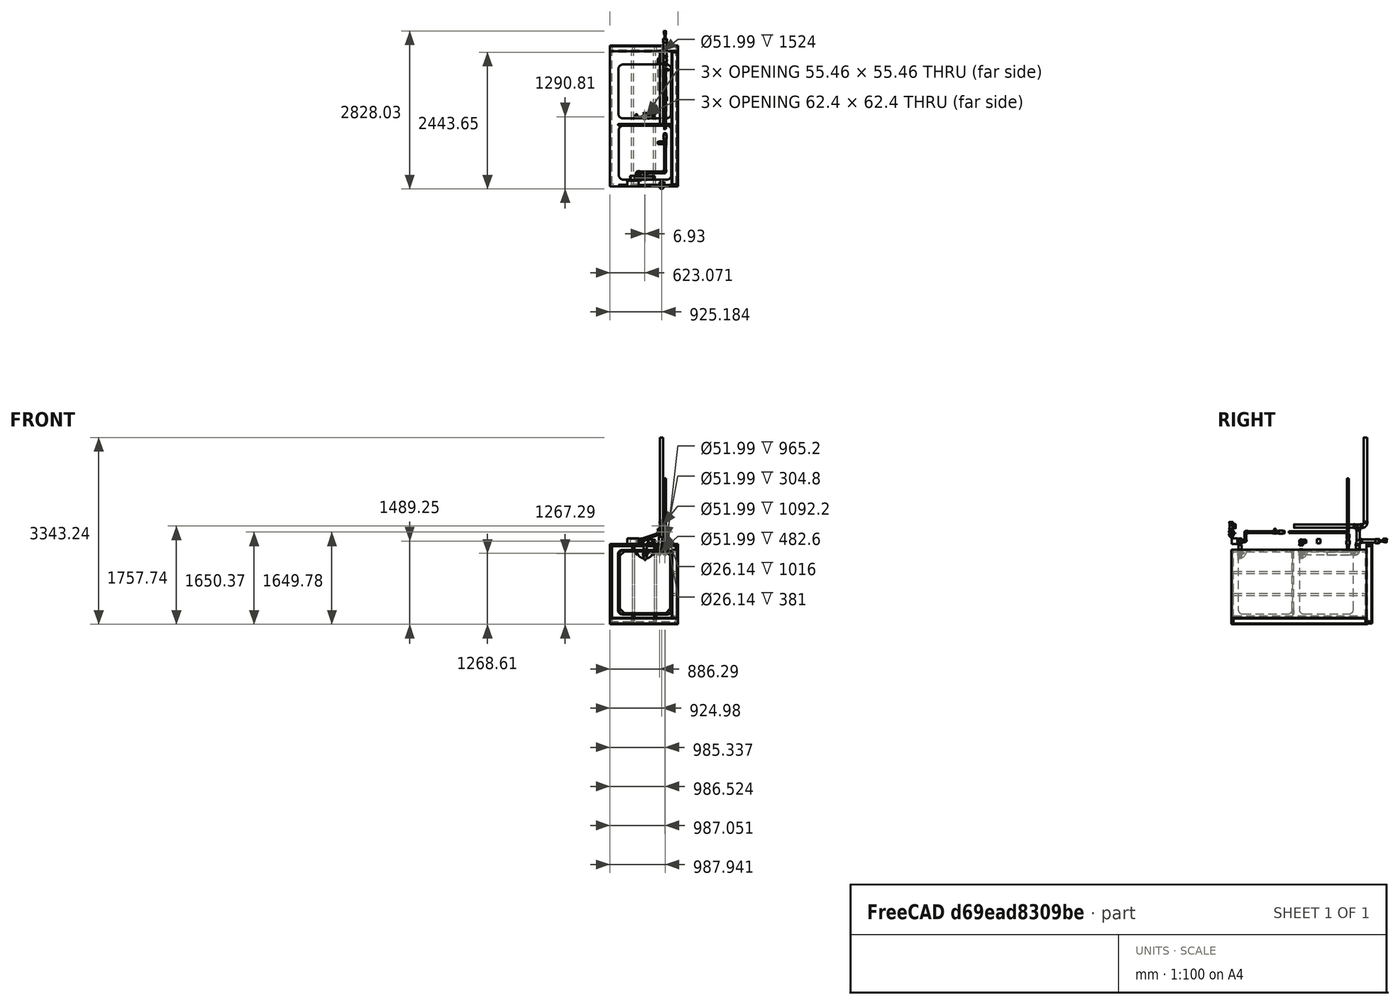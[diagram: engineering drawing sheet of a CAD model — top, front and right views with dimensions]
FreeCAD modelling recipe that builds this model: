
FCSTD DOCUMENT  (FreeCAD 0.17R13125 (Git))
Label: biodigester with case
License: All rights reserved
LicenseURL: http://en.wikipedia.org/wiki/All_rights_reserved
objects: Part::FeaturePython×50, Part::Feature×29, Part::Compound×2, Part::Box×1, Part::Cylinder×1, Part::Cut×1, App::MeasureDistance×1
note: 84 computed .brp shape members not serialized (recipe doc carries the construction recipe); baked Part::Feature solids carry a one-line shape summary decoded from their .brp

FEATURE [Part::Feature] Part__Feature  label="Waste Elbow 2"
  Placement = pos=(292.227,-26.6835,668.11) rot=(0,1,0;1.5708rad)
  shape: bbox 74.37 x 115.1 x 115.1 mm, 30 faces (baked)
FEATURE [Part::Feature] Part__Feature016  label="Bottom Tee"
  Placement = pos=(-0.557936,130.762,666.483) rot=(0,0.707107,-0.707107;3.14159rad)
  shape: bbox 131.8 x 74.37 x 115.1 mm, 49 faces (baked)
FEATURE [Part::Feature] Part__Feature017  label="Tee to pump Bushing"
  Placement = pos=(-111.322,130.762,666.828) rot=(0,1,0;3.14159rad)
  shape: bbox 44.45 x 100.1 x 100.1 mm, 12 faces (baked)
FEATURE [Part::Feature] pipe__solid_  label="Pipe to Pump"
  Placement = pos=(-130.733,130.762,666.483) rot=(0,1,0;1.5708rad)
  shape: bbox 76.2 x 60.33 x 60.33 mm, 4 faces (baked)
FEATURE [Part::FeaturePython] Clone001  label="Top Tote"  # WARN: FeaturePython — macro-defined, semantics opaque (R4)
  AttacherType = Attacher::AttachEngine3D
  Fuse = false
  MapMode = -1
  Placement = pos=(-8.60907,1092.95,-66.7069) rot=(0,0,1;0rad)
  Scale = (1,1,1)
FEATURE [Part::FeaturePython] Clone  label="Bottom Tote"  # WARN: FeaturePython — macro-defined, semantics opaque (R4)
  AttacherType = Attacher::AttachEngine3D
  Fuse = false
  MapMode = -1
  Placement = pos=(-1.679,-2.02686,-66.7069) rot=(0,0,1;0rad)
  Scale = (1,1,1)
FEATURE [Part::FeaturePython] Clone002  label="Macerator Lift Pump001"  # WARN: FeaturePython — macro-defined, semantics opaque (R4)
  AttacherType = Attacher::AttachEngine3D
  Fuse = false
  MapMode = -1
  Placement = pos=(-116.31,128.621,668.824) rot=(0,-1,0;1.5708rad)
  Scale = (1,1,1)
FEATURE [Part::Box] Box  label="C"
  AttacherType = Attacher::AttachEngine3D
  Height = 101.6
  Length = 203.2
  Placement = pos=(-317.752,-21.356,614.794) rot=(0,0,1;0rad)
  Width = 101.6
FEATURE [Part::FeaturePython] Clone003  label="bottom 2" tee"  # Draft clone (typed FeaturePython)
  Objects = -> [Part__Feature016]
  Placement = pos=(144.238,131.333,666.304) rot=(0,0.99998,-0.006329;3.14159rad)
  Scale = (1,1,1)
FEATURE [Part::FeaturePython] Clone004  label="Waste 2" elbow"  # Draft clone (typed FeaturePython)
  Objects = -> [Part__Feature]
  Placement = pos=(293.076,131.009,668.16) rot=(1,0,0;3.14159rad)
  Scale = (1,1,1)
FEATURE [Part::Feature] pipe__solid_001  label="Waste Pipe"
  Placement = pos=(292.227,-26.6835,745.898) rot=(0,0,1;0rad)
  shape: bbox 60.33 x 60.33 x 1524 mm, 4 faces (baked)
FEATURE [Part::FeaturePython] Clone007  label="Top Elbow 1"  # WARN: FeaturePython — macro-defined, semantics opaque (R4)
  Placement = pos=(-7.45656,1223.7,666.865) rot=(0,0.707107,-0.707107;3.14159rad)
  Scale = (1,1,1)
FEATURE [Part::Feature] pipe__solid_002  label="Up pipe"
  Placement = pos=(145.662,1171.16,668.091) rot=(1,0,0;1.5708rad)
  shape: bbox 60.33 x 965.2 x 60.33 mm, 4 faces (baked)
FEATURE [Part::Feature] pipe__solid_003  label="Drain stub 2""
  Placement = pos=(127.656,129.545,666.053) rot=(0,-1,0;1.5708rad)
  shape: bbox 76.2 x 60.33 x 60.33 mm, 4 faces (baked)
FEATURE [Part::FeaturePython] Clone010  label="Top Cleanout Tee"  # Draft clone (typed FeaturePython)
  Objects = -> [Clone003]
  Placement = pos=(147.691,1224.35,665.907) rot=(0.006329,0.006329,0.99996;1.57084rad)
  Scale = (1,1,1)
FEATURE [Part::FeaturePython] Clone011  label="2" valve"  # WARN: FeaturePython — macro-defined, semantics opaque (R4)
  Scale = (1,1,1)
FEATURE [Part::Feature] pipe__solid_004  label="pipe (solid)"
  Placement = pos=(254.718,597.22,447.562) rot=(-1,0,0;1.5708rad)
  shape: bbox 60.33 x 482.6 x 60.33 mm, 4 faces (baked)
FEATURE [Part::FeaturePython] Clone013  label="Waste 2" elbow001"  # Draft clone (typed FeaturePython)
  AttacherType = Attacher::AttachEngine3D
  Fuse = false
  MapMode = -1
  Objects = -> [Clone004]
  Placement = pos=(293.076,131.009,668.16) rot=(1,0,0;3.14159rad)
  Scale = (1,1,1)
FEATURE [Part::FeaturePython] Clone015  label="Overflow Tee"  # Draft clone (typed FeaturePython)
  AttacherType = Attacher::AttachEngine3D
  Fuse = false
  MapMode = -1
  Objects = -> [Clone010]
  Placement = pos=(293.218,1148.28,936.413) rot=(-0.564425,-0.564425,0.602369;2.05727rad)
  Scale = (1,1,1)
FEATURE [Part::FeaturePython] Clone014  label="Gas Elbow"  # Draft clone (typed FeaturePython)
  AttacherType = Attacher::AttachEngine3D
  Fuse = false
  MapMode = -1
  Objects = -> [Clone013]
  Placement = pos=(355.154,1146.76,448.742) rot=(0.707107,0,-0.707107;3.14159rad)
  Scale = (1,1,1)
FEATURE [Part::FeaturePython] Clone016  label="Overflow Tee 2"  # Draft clone (typed FeaturePython)
  AttacherType = Attacher::AttachEngine3D
  Fuse = false
  MapMode = -1
  Objects = -> [Clone015]
  Placement = pos=(292.224,-26.2791,935.756) rot=(0.006329,0.99996,-0.006329;1.57084rad)
  Scale = (1,1,1)
FEATURE [Part::FeaturePython] Clone017  label="Gas Downpipe"  # Draft clone (typed FeaturePython)
  AttacherType = Attacher::AttachEngine3D
  Fuse = false
  MapMode = -1
  Objects = -> [pipe__solid_002]
  Placement = pos=(354.629,1072.64,448.875) rot=(1,0,0;1.5708rad)
  Scale = (1,1,1)
FEATURE [Part::Cylinder] Cylinder
  Angle = 360
  AttacherType = Attacher::AttachEngine3D
  Height = 127
  Placement = pos=(353.737,1033.4,387.109) rot=(0,0,1;0rad)
  Radius = 21.59
FEATURE [Part::Cut] Cut  label="Gas Cut Pipe"
  Base = -> Clone017
  Refine = true
  Tool = -> Cylinder
FEATURE [Part::FeaturePython] Clone018  label="Gas Elbow 2"  # Draft clone (typed FeaturePython)
  AttacherType = Attacher::AttachEngine3D
  Fuse = false
  MapMode = -1
  Objects = -> [Clone014]
  Placement = pos=(355.824,1146.66,669.178) rot=(0,-1,0;1.5708rad)
  Scale = (1,1,1)
FEATURE [Part::Feature] pipe__solid_005  label="Gas Out Stub"
  Placement = pos=(354.597,1146.35,508.528) rot=(0,0,1;0rad)
  shape: bbox 60.33 x 60.33 x 101.6 mm, 4 faces (baked)
FEATURE [Part::Feature] pipe__solid_006  label="Gas Out"
  Placement = pos=(355.816,1528.26,669.516) rot=(1,0,0;1.5708rad)
  shape: bbox 60.33 x 304.8 x 60.33 mm, 4 faces (baked)
FEATURE [Part::Feature] pipe__solid_007  label="Gas Out 1/2""
  Placement = pos=(355.659,1655.7,669.196) rot=(1,0,0;1.5708rad)
  shape: bbox 21.34 x 152.4 x 21.34 mm, 4 faces (baked)
FEATURE [Part::Feature] pipe__solid_008  label="Effluent Down Pipe"
  Placement = pos=(293.409,0.694018,938.006) rot=(-1,0,0;1.5708rad)
  shape: bbox 60.33 x 1092 x 60.33 mm, 4 faces (baked)
FEATURE [Part::Feature] pipe__solid_009  label="Effluent Horizontal Pipe"
  Placement = pos=(261.486,1148.14,525.53) rot=(0,1,0;0.069813rad)
  shape: bbox 86.76 x 60.33 x 384.3 mm, 4 faces (baked)
FEATURE [Part::FeaturePython] Clone025  label="Gas Out001"  # Draft clone (typed FeaturePython)
  AttacherType = Attacher::AttachEngine3D
  Fuse = false
  MapMode = -1
  Objects = -> [pipe__solid_006]
  Placement = pos=(355.816,1528.26,669.516) rot=(1,0,0;1.5708rad)
  Scale = (1,1,1)
FEATURE [Part::FeaturePython] Clone026  label="Gas Out 1/2"001"  # Draft clone (typed FeaturePython)
  AttacherType = Attacher::AttachEngine3D
  Fuse = false
  MapMode = -1
  Objects = -> [pipe__solid_007]
  Placement = pos=(355.659,1620.29,670.928) rot=(1,0,0;1.5708rad)
  Scale = (1,1,1)
FEATURE [Part::FeaturePython] Clone027  label="Gas Elbow 003"  # Draft clone (typed FeaturePython)
  AttacherType = Attacher::AttachEngine3D
  Fuse = false
  MapMode = -1
  Objects = -> [Clone018]
  Placement = pos=(355.824,1146.66,669.178) rot=(0,-1,0;1.5708rad)
  Scale = (1,1,1)
FEATURE [Part::FeaturePython] Clone028  label="Gas Elbow 004"  # Draft clone (typed FeaturePython)
  AttacherType = Attacher::AttachEngine3D
  Fuse = false
  MapMode = -1
  Objects = -> [Clone018]
  Placement = pos=(355.824,1146.66,669.178) rot=(0,-1,0;1.5708rad)
  Scale = (1,1,1)
FEATURE [Part::FeaturePython] Clone029  label="Gas Out Stub001"  # Draft clone (typed FeaturePython)
  AttacherType = Attacher::AttachEngine3D
  Fuse = false
  MapMode = -1
  Objects = -> [pipe__solid_005]
  Placement = pos=(354.597,1146.35,508.528) rot=(0,0,1;0rad)
  Scale = (1,1,1)
FEATURE [Part::FeaturePython] Clone030  label="Gas Elbow001"  # Draft clone (typed FeaturePython)
  AttacherType = Attacher::AttachEngine3D
  Fuse = false
  MapMode = -1
  Objects = -> [Clone014]
  Placement = pos=(355.154,1146.76,448.742) rot=(0.707107,0,-0.707107;3.14159rad)
  Scale = (1,1,1)
FEATURE [Part::FeaturePython] Clone031  label="Gas Cut Pipe001"  # Draft clone (typed FeaturePython)
  AttacherType = Attacher::AttachEngine3D
  Fuse = false
  MapMode = -1
  Objects = -> [Cut]
  Scale = (1,1,1)
FEATURE [Part::Compound] Compound001  label="Top Gas Out"
  Links = -> [Clone031,Clone030,Clone029,Clone028,Clone027,Clone026,Clone025]
  Placement = pos=(-0.971954,1087.98,0) rot=(0,0,1;0rad)
FEATURE [Part::FeaturePython] Clone032  label="Effluent Elbow Orig"  # Draft clone (typed FeaturePython)
  AttacherType = Attacher::AttachEngine3D
  Fuse = false
  MapMode = -1
  Objects = -> [Clone014]
  Placement = pos=(254.97,1146.76,448.515) rot=(-0.681998,0,0.731354;3.14159rad)
  Scale = (1,1,1)
FEATURE [Part::FeaturePython] Clone033  label="pipe (solid)001"  # Draft clone (typed FeaturePython)
  AttacherType = Attacher::AttachEngine3D
  Fuse = false
  MapMode = -1
  Objects = -> [pipe__solid_004]
  Placement = pos=(254.718,597.22,447.562) rot=(-1,0,0;1.5708rad)
  Scale = (1,1,1)
FEATURE [Part::FeaturePython] Clone034  label="Effluent Elbow Orig001"  # Draft clone (typed FeaturePython)
  AttacherType = Attacher::AttachEngine3D
  Fuse = false
  MapMode = -1
  Objects = -> [Clone032]
  Placement = pos=(254.97,1146.76,448.515) rot=(-0.681998,0,0.731354;3.14159rad)
  Scale = (1,1,1)
FEATURE [Part::FeaturePython] Clone035  label="Effluent Horizontal Pipe001"  # Draft clone (typed FeaturePython)
  AttacherType = Attacher::AttachEngine3D
  Fuse = false
  MapMode = -1
  Objects = -> [pipe__solid_009]
  Placement = pos=(261.486,1148.14,525.53) rot=(0,1,0;0.069813rad)
  Scale = (1,1,1)
FEATURE [Part::FeaturePython] Clone036  label="Overflow Tee001"  # Draft clone (typed FeaturePython)
  AttacherType = Attacher::AttachEngine3D
  Fuse = false
  MapMode = -1
  Objects = -> [Clone015]
  Placement = pos=(293.218,1148.28,936.413) rot=(-0.564425,-0.564425,0.602369;2.05727rad)
  Scale = (1,1,1)
FEATURE [Part::FeaturePython] Clone037  label="Effluent Down Pipe001"  # Draft clone (typed FeaturePython)
  AttacherType = Attacher::AttachEngine3D
  Fuse = false
  MapMode = -1
  Objects = -> [pipe__solid_008]
  Placement = pos=(293.409,0.694018,938.006) rot=(-1,0,0;1.5708rad)
  Scale = (1,1,1)
FEATURE [Part::Compound] Compound  label="Top Effluent"
  Links = -> [Clone037,Clone036,Clone035,Clone034,Clone033]
  Placement = pos=(-0.108429,1095.21,0) rot=(0,0,1;0rad)
FEATURE [Part::Feature] Part__Feature018  label="1" Check Valve"
  Placement = pos=(356.496,968.917,636.21) rot=(0,0,1;0rad)
  shape: bbox 63.23 x 63.23 x 130.2 mm, 192 faces (baked)
FEATURE [Part::FeaturePython] Clone038  label="1" Check Valve 2"  # Draft clone (typed FeaturePython)
  AttacherType = Attacher::AttachEngine3D
  Fuse = false
  MapMode = -1
  Objects = -> [Part__Feature018]
  Placement = pos=(354.272,2063.31,639.561) rot=(0,0,1;0rad)
  Scale = (1,1,1)
FEATURE [Part::Feature] Part__Feature019  label="Tee"
  Placement = pos=(356.759,970.863,829.265) rot=(0.57735,0.57735,-0.57735;4.18879rad)
  shape: bbox 40.67 x 84.99 x 62.83 mm, 22 faces (baked)
FEATURE [Part::Feature] Part__Feature003  label="valve"
  Placement = pos=(356.4,1013.02,829.485) rot=(-0.57735,-0.57735,0.57735;4.18879rad)
  shape: bbox 89.47 x 89.46 x 56.7 mm, 221 faces (baked)
FEATURE [Part::FeaturePython] Clone039  label="valve001"  # Draft clone (typed FeaturePython)
  AttacherType = Attacher::AttachEngine3D
  Fuse = false
  MapMode = -1
  Objects = -> [Part__Feature003]
  Placement = pos=(356.4,969.897,702.526) rot=(0.707107,0.707107,0;3.14159rad)
  Scale = (1,1,1)
FEATURE [Part::Feature] pipe__solid_010  label="pipe (solid)002"
  Placement = pos=(354.889,2063.12,703.573) rot=(0,0,1;0rad)
  shape: bbox 33.4 x 33.4 x 101.6 mm, 4 faces (baked)
FEATURE [Part::FeaturePython] Clone040  label="Clone of valve001"  # Draft clone (typed FeaturePython)
  Objects = -> [Clone039]
  Placement = pos=(356.4,2062.96,704.38) rot=(0.707107,0.707107,0;3.14159rad)
  Scale = (1,1,1)
FEATURE [Part::FeaturePython] Clone041  label="Clone of Tee"  # Draft clone (typed FeaturePython)
  Objects = -> [Part__Feature019]
  Placement = pos=(356.759,2061.9,829.935) rot=(0.707107,0,-0.707107;3.14159rad)
  Scale = (1,1,1)
FEATURE [Part::FeaturePython] Clone043  label="Clone of 1" Check Valve"  # Draft clone (typed FeaturePython)
  Objects = -> [Part__Feature018]
  Placement = pos=(356.496,863.855,829.357) rot=(1,0,0;1.5708rad)
  Scale = (1,1,1)
FEATURE [Part::FeaturePython] Clone044  label="Main Inlet Pipe"  # WARN: FeaturePython — macro-defined, semantics opaque (R4)
  Placement = pos=(357.263,2095.31,774.716) rot=(0,0,1;0rad)
  Scale = (1,1,1)
FEATURE [Part::Feature] Part__Feature008  label="reducer001"
  Placement = pos=(356.017,712.129,830.191) rot=(0.707107,0.707107,0;3.14159rad)
  shape: bbox 38.57 x 31.75 x 33.4 mm, 21 faces (baked)
FEATURE [Part::Feature] pipe__solid_011  label="pipe (solid)003"
  Placement = pos=(356.065,701.72,830) rot=(1,0,0;1.5708rad)
  shape: bbox 26.67 x 50.8 x 26.67 mm, 4 faces (baked)
FEATURE [Part::Feature] Part__Feature001  label="elbow"
  Placement = pos=(355.287,228.96,830.537) rot=(1e-06,-1,0;0.287855rad)
  shape: bbox 70.13 x 66.28 x 52.72 mm, 15 faces (baked)
FEATURE [Part::Feature] Part__Feature020  label="elbow001"
  Placement = pos=(-146.156,227.436,670.19) rot=(0.702694,0.702694,0.111546;2.91942rad)
  shape: bbox 70.28 x 66.28 x 53.74 mm, 15 faces (baked)
FEATURE [Part::Feature] pipe__solid_012  label="pipe (solid)004"
  Placement = pos=(-102.381,227.436,684.447) rot=(0,1,0;1.25594rad)
  shape: bbox 420.9 x 33.4 x 165.5 mm, 4 faces (baked)
FEATURE [Part::Feature] pipe__solid_014  label="pipe (solid)006"
  Placement = pos=(355.371,2019.41,830.64) rot=(1,0,0;1.5708rad)
  shape: bbox 33.4 x 1016 x 33.4 mm, 4 faces (baked)
FEATURE [Part::FeaturePython] Clone047  label="Clone of Gas Elbow 2"  # Draft clone (typed FeaturePython)
  Objects = -> [Clone018]
  Placement = pos=(292.773,2375.64,935.895) rot=(0.57735,0.57735,0.57735;2.0944rad)
  Scale = (1,1,1)
FEATURE [Part::FeaturePython] Clone048  label="Clone of Waste Pipe"  # Draft clone (typed FeaturePython)
  Objects = -> [pipe__solid_001]
  Placement = pos=(293.504,2375.79,999.508) rot=(0,0,1;0rad)
  Scale = (1,1,1)
FEATURE [Part::FeaturePython] Screw  label="Screw Cap"  # Fasteners workbench fastener (typed FeaturePython)
  Placement = pos=(148.795,1298.82,662.856) rot=(-1,0,0;1.5708rad)
  diameter = 19
  invert = false
  length = 0
  matchOuter = false
  offset = 0
  thread = false
  type = 14
FEATURE [Part::Feature] Part__Feature021  label="4880K338"
  Placement = pos=(356.246,1543.7,668.93) rot=(0.57735,-0.57735,0.57735;4.18879rad)
  shape: bbox 61.91 x 39.69 x 71.49 mm, 16 faces (baked)
FEATURE [Part::Feature] pipe__solid_017  label="pipe (solid)009"
  Placement = pos=(356.77,1570.05,668.934) rot=(1,0,0;1.5708rad)
  shape: bbox 73.03 x 63.5 x 73.03 mm, 4 faces (baked)
FEATURE [Part::FeaturePython] Clone049  label="Clone of pipe (solid)009"  # Draft clone (typed FeaturePython)
  Objects = -> [pipe__solid_017]
  Placement = pos=(356.77,1570.05,668.934) rot=(1,0,0;1.5708rad)
  Scale = (1,1,1)
FEATURE [Part::FeaturePython] Clone051  label="Clone of pipe (solid)010"  # Draft clone (typed FeaturePython)
  Objects = -> [pipe__solid_017]
  Placement = pos=(354.821,2613.44,668.934) rot=(1,0,0;1.5708rad)
  Scale = (1,1,1)
FEATURE [Part::FeaturePython] Clone052  label="Clone of 4880K339"  # Draft clone (typed FeaturePython)
  Objects = -> [Part__Feature021]
  Placement = pos=(354.297,2587.09,668.93) rot=(0.57735,-0.57735,0.57735;4.18879rad)
  Scale = (1,1,1)
FEATURE [Part::Feature] Part__Feature022  label="4876K81"
  Placement = pos=(356.033,1647.5,668.901) rot=(1,0,0;1.5708rad)
  shape: bbox 39.52 x 69.69 x 62.62 mm, 221 faces (baked)
FEATURE [Part::FeaturePython] Clone053  label="Top Gas Valve"  # Draft clone (typed FeaturePython)
  Objects = -> [Part__Feature022]
  Placement = pos=(354.219,2691.59,668.901) rot=(1,0,0;1.5708rad)
  Scale = (1,1,1)
FEATURE [Part::FeaturePython] Clone054  label="Cleanout Cap"  # Draft clone (typed FeaturePython)
  Objects = -> [Part__Feature021]
  Placement = pos=(147.882,1261.83,665.068) rot=(0.57735,-0.57735,0.57735;4.18879rad)
  Scale = (1,1,1)
FEATURE [Part::FeaturePython] Clone055  label="Pumpout Tee"  # Draft clone (typed FeaturePython)
  AttacherType = Attacher::AttachEngine3D
  Fuse = false
  MapMode = -1
  Objects = -> [Clone041]
  Placement = pos=(355.095,755.584,829.996) rot=(0.707107,-0.707107,0;3.14159rad)
  Scale = (1,1,1)
FEATURE [Part::Feature] pipe__solid_019  label="Circulating Pipe 2"
  Placement = pos=(356.261,274.703,830.046) rot=(-1,0,0;1.5708rad)
  shape: bbox 33.4 x 381 x 33.4 mm, 4 faces (baked)
FEATURE [Part::FeaturePython] Clone056  label="Pumped Exit Valve"  # Draft clone (typed FeaturePython)
  AttacherType = Attacher::AttachEngine3D
  Fuse = false
  MapMode = -1
  Objects = -> [Clone039]
  Placement = pos=(228.429,755.677,829.394) rot=(0.57735,-0.57735,-0.57735;2.0944rad)
  Scale = (1,1,1)
FEATURE [Part::FeaturePython] Clone058  label="Front Panel"  # WARN: FeaturePython — macro-defined, semantics opaque (R4)
  AttacherType = Attacher::AttachEngine3D
  Fuse = false
  MapMode = -1
  Placement = pos=(-127.546,1838.58,515.569) rot=(0,-1,0;1.5708rad)
  Scale = (1,1,1)
FEATURE [Part::FeaturePython] Clone059  label="Left Panel"  # Draft clone (typed FeaturePython)
  Objects = -> [Clone058]
  Placement = pos=(-631.743,1838.62,9.57407) rot=(0,0,1;0rad)
  Scale = (1,1,1)
FEATURE [Part::FeaturePython] Clone060  label="Back Panel"  # Draft clone (typed FeaturePython)
  Objects = -> [Clone058]
  Placement = pos=(-128.488,1838.58,-819.73) rot=(0,-1,0;1.5708rad)
  Scale = (1,1,1)
FEATURE [Part::FeaturePython] Clone061  label="Right Panel"  # Draft clone (typed FeaturePython)
  Objects = -> [Clone059]
  Placement = pos=(473.044,1838.62,11.4596) rot=(0,0,1;0rad)
  Scale = (1,1,1)
FEATURE [Part::FeaturePython] Clone005  label="Top Panel"  # WARN: FeaturePython — macro-defined, semantics opaque (R4)
  Placement = pos=(85.8099,2497.78,-1246.56) rot=(-0.57735,0.57735,-0.57735;2.0944rad)
  Scale = (1,1,1)
FEATURE [Part::Feature] pipe__solid_020  label="Top Digester - Bung Pipe"
  Placement = pos=(-7.66051,1223.88,521.742) rot=(0,0,1;0rad)
  shape: bbox 60.33 x 60.33 x 76.2 mm, 4 faces (baked)
FEATURE [Part::FeaturePython] Clone062  label="Bottom Digester - Bung Pipe"  # Draft clone (typed FeaturePython)
  AttacherType = Attacher::AttachEngine3D
  Fuse = false
  Objects = -> [pipe__solid_020]
  Placement = pos=(-0.886756,130.357,523.199) rot=(0,0,1;0rad)
  Scale = (1,1,1)
FEATURE [Part::Feature] pipe__solid_021  label="Circulation Inlet Pipe 1"
  Placement = pos=(355.668,969.751,496.212) rot=(0,0,1;0rad)
  shape: bbox 33.4 x 33.4 x 76.2 mm, 4 faces (baked)
FEATURE [Part::FeaturePython] Clone063  label="Circulation Inlet Pipe 002"  # Draft clone (typed FeaturePython)
  AttacherType = Attacher::AttachEngine3D
  Fuse = false
  Objects = -> [pipe__solid_021]
  Placement = pos=(355.668,2062.28,497.014) rot=(0,0,1;0rad)
  Scale = (1,1,1)
FEATURE [App::MeasureDistance] Distance  label="Distance: 9.18 in"
  Distance = 233.094
  P1 = (264.338,2267.47,824.92)
  P2 = (335.705,2048.67,787.962)
